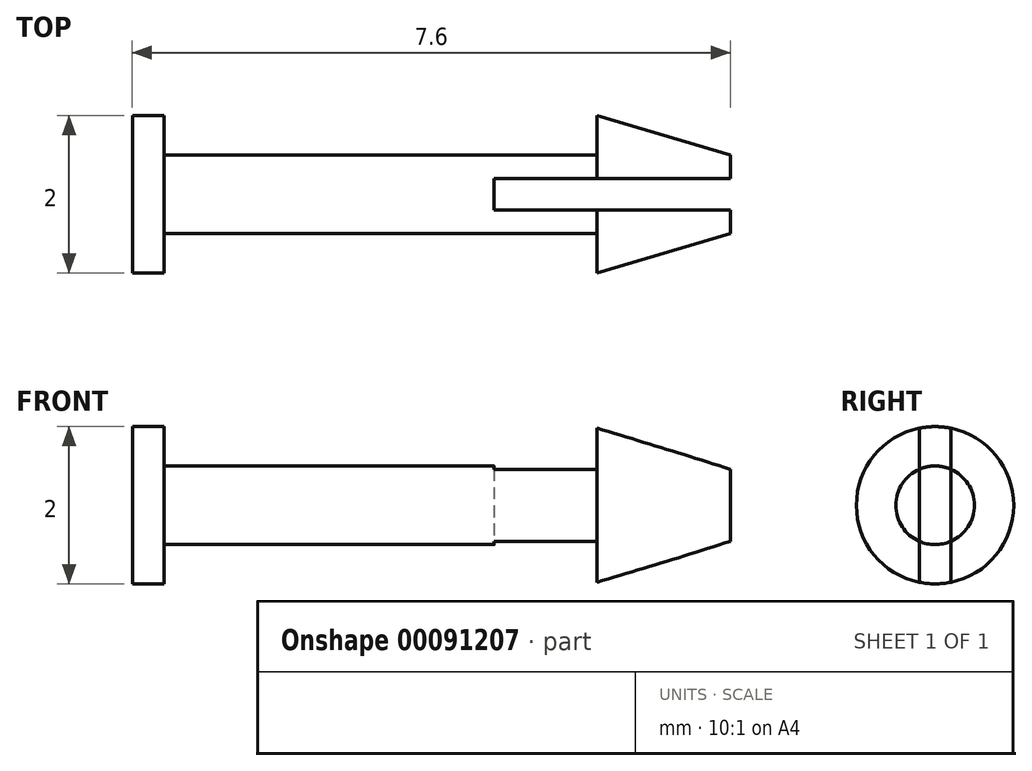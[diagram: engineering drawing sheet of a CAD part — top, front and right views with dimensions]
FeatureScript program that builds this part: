
annotation { "Feature Type Name" : "Feature", "Feature Type Description" : "" }
export const myFeature = defineFeature(function(context is Context, id is Id, definition is map)
    precondition{}
    {
        {
            var Q0;
            Q0=qCreatedBy(makeId("Front.planeOp"),FACE);
            var sketch = newSketch(context, id + "F0", { "sketchPlane" : qUnion([Q0])});
            skLineSegment(sketch, "E0", {"start": v(-7.2, 0) * mm, "end": v(-7.2, -0.5) * mm});
            skLineSegment(sketch, "E1", {"start": v(-7.2, -0.5) * mm, "end": v(-7.6, -0.5) * mm});
            skLineSegment(sketch, "E2", {"start": v(-7.6, -0.5) * mm, "end": v(-7.6, 0.5) * mm});
            skLineSegment(sketch, "E3", {"start": v(-7.6, 0.5) * mm, "end": v(0, 0.5) * mm});
            skLineSegment(sketch, "E4", {"start": v(-7.2, 0) * mm, "end": v(-1.7, 0) * mm});
            skLineSegment(sketch, "E5", {"start": v(-1.7, 0) * mm, "end": v(-1.7, -0.5) * mm});
            skLineSegment(sketch, "E6", {"start": v(0, 0.5) * mm, "end": v(0, 0) * mm});
            skLineSegment(sketch, "E7", {"start": v(0, 0) * mm, "end": v(-1.7, -0.5) * mm});
            skSolve(sketch);
        }
        {
            var Q0;
            Q0 = qSketchRegion(id + "F0", true);
            var Q1;
            Q1=sQuery(id+"F0.wireOp",EDGE,"E3");
            revolve(context, id + "F1", {"entities" : qUnion([Q0]), "axis" : qUnion([Q1]), "revolveType" : RevolveType.FULL});
        }
        {
            var Q0;
            Q0=qCreatedBy(makeId("Right.planeOp"),FACE);
            var sketch = newSketch(context, id + "F2", { "sketchPlane" : qUnion([Q0])});
            skLineSegment(sketch, "E8.bottom", {"start": v(-0.2, 1.6) * mm, "end": v(0.2, 1.6) * mm});
            skLineSegment(sketch, "E8.top", {"start": v(-0.2, -1.6) * mm, "end": v(0.2, -1.6) * mm});
            skLineSegment(sketch, "E8.left", {"start": v(-0.2, 1.6) * mm, "end": v(-0.2, -1.6) * mm});
            skLineSegment(sketch, "E8.right", {"start": v(0.2, 1.6) * mm, "end": v(0.2, -1.6) * mm});
            skPoint(sketch, "E8.middle", {"position": v(0, 0) * mm});
            skSolve(sketch);
        }
        {
            var Q0;
            Q0 = qSketchRegion(id + "F2", true);
            extrude(context, id + "F3", {"entities" : qUnion([Q0]), "operationType" : NewBodyOperationType.REMOVE, "oppositeDirection" : true, "depth" : 3 * mm});
        }
    });
